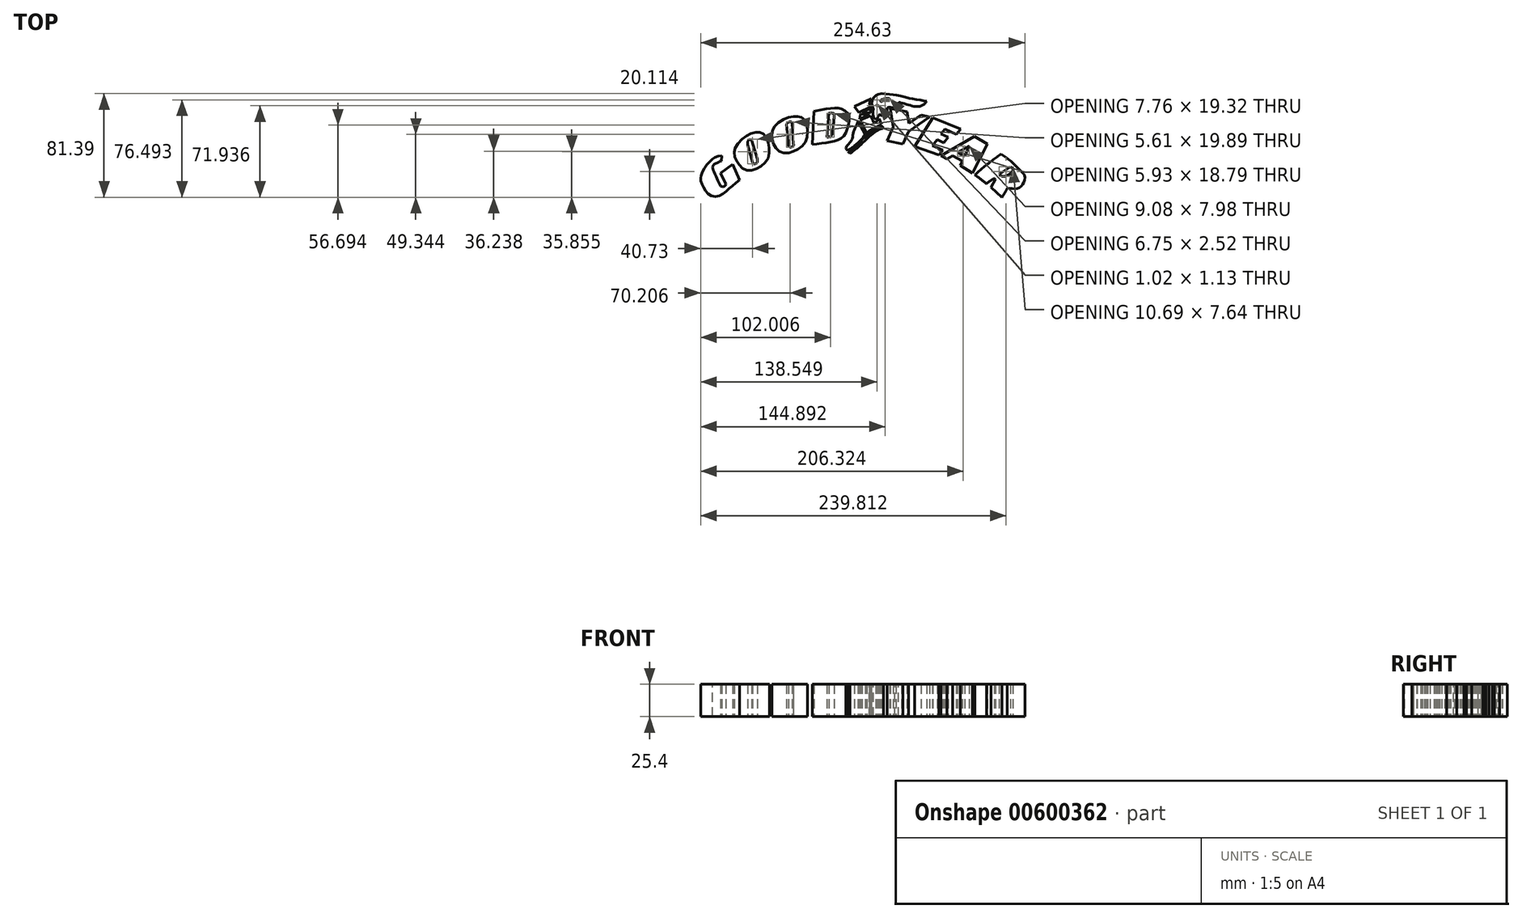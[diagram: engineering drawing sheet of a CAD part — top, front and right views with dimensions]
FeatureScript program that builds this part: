
annotation { "Feature Type Name" : "Feature", "Feature Type Description" : "" }
export const myFeature = defineFeature(function(context is Context, id is Id, definition is map)
    precondition{}
    {
        {
            var Q0;
            Q0=qCreatedBy(makeId("Top.planeOp"),FACE);
            var sketch = newSketch(context, id + "F0", { "sketchPlane" : qUnion([Q0])});
            skFitSpline(sketch, "E0", {"points": [v(-59.77, 19.65) * mm, v(-63.83, 18.9) * mm, v(-66.56, 17.29) * mm, v(-70.08, 14) * mm, v(-73.2, 9.83) * mm, v(-75.73, 4.75) * mm, v(-76.25, 2.47) * mm, v(-76.18, 0) * mm, v(-74.98, -3.55) * mm, v(-72.37, -7.96) * mm, v(-69.17, -11.16) * mm, v(-64.56, -12.56) * mm, v(-59.15, -10.76) * mm, v(-55.35, -7.59) * mm, v(-51.14, -3.95) * mm, v(-45.8, 0.36) * mm], "startDerivative": vector(-48.72, 2.07) * mm, "endDerivative": vector(63.75, 50.3) * mm});
            skLineSegment(sketch, "E1", {"start": v(-59.77, 19.65) * mm, "end": v(-59.86, 15.48) * mm});
            skLineSegment(sketch, "E2", {"start": v(-45.8, 0.36) * mm, "end": v(-51.25, 12.96) * mm});
            skLineSegment(sketch, "E3", {"start": v(-51.25, 12.96) * mm, "end": v(-60.63, 5.88) * mm});
            skLineSegment(sketch, "E4", {"start": v(-60.63, 5.88) * mm, "end": v(-56.41, -2.7) * mm});
            skFitSpline(sketch, "E5", {"points": [v(-59.86, 15.48) * mm, v(-62.4, 14.45) * mm, v(-64.42, 13.43) * mm, v(-66.28, 12.15) * mm, v(-66.87, 9.93) * mm, v(-66.03, 7.47) * mm, v(-64, 2.8) * mm, v(-62.32, -0.84) * mm, v(-61.06, -3.39) * mm, v(-60.55, -4.32) * mm, v(-58.95, -4.91) * mm, v(-57.09, -4.06) * mm, v(-56.41, -2.7) * mm], "startDerivative": vector(-29.78, -11.35) * mm, "endDerivative": vector(6.97, 21.82) * mm});
            skFitSpline(sketch, "E6", {"points": [v(-49.9, 22.3) * mm, v(-48.7, 26.42) * mm, v(-44.08, 32.4) * mm, v(-38.41, 36.27) * mm, v(-33.27, 38.01) * mm, v(-29.32, 37.9) * mm, v(-25.5, 35.12) * mm, v(-23.13, 29.56) * mm, v(-22.34, 23.86) * mm, v(-23.27, 17.75) * mm, v(-27.62, 12.43) * mm, v(-32.9, 9.1) * mm, v(-38.3, 7.89) * mm, v(-43.44, 9.73) * mm, v(-46.87, 13.56) * mm, v(-48.97, 17.14) * mm, v(-49.9, 22.3) * mm]});
            skLineSegment(sketch, "E7", {"start": v(-36.05, 31.72) * mm, "end": v(-31.85, 16.84) * mm});
            skLineSegment(sketch, "E8", {"start": v(-39.36, 28.04) * mm, "end": v(-35.4, 14.58) * mm});
            skFitSpline(sketch, "E9", {"points": [v(-39.36, 28.04) * mm, v(-39.36, 30.3) * mm, v(-38.28, 31.96) * mm, v(-36.88, 32.38) * mm, v(-36.05, 31.72) * mm], "startDerivative": vector(-0.89, 7.93) * mm, "endDerivative": vector(3.61, -4.33) * mm});
            skFitSpline(sketch, "E10", {"points": [v(-31.85, 16.84) * mm, v(-31.85, 14.17) * mm, v(-33.09, 13.34) * mm, v(-34.41, 13.08) * mm, v(-35.4, 14.58) * mm], "startDerivative": vector(1.44, -10.29) * mm, "endDerivative": vector(-1.3, 7.85) * mm});
            skLineSegment(sketch, "E11", {"start": v(-8.9, 44.2) * mm, "end": v(-7.35, 27.45) * mm});
            skLineSegment(sketch, "E12", {"start": v(-4.4, 45.2) * mm, "end": v(-3.4, 28.77) * mm});
            skFitSpline(sketch, "E13", {"points": [v(-8.9, 44.2) * mm, v(-8.13, 45.2) * mm, v(-6.65, 46.05) * mm, v(-5.18, 46.05) * mm, v(-4.4, 45.2) * mm], "startDerivative": vector(2.8, 4.36) * mm, "endDerivative": vector(2.83, -4.51) * mm});
            skFitSpline(sketch, "E14", {"points": [v(-7.35, 27.45) * mm, v(-6.5, 26.52) * mm, v(-5.65, 26.29) * mm, v(-4.64, 26.44) * mm, v(-3.4, 27.3) * mm, v(-3.4, 28.77) * mm], "startDerivative": vector(3.78, -5) * mm, "endDerivative": vector(-0.95, 4.32) * mm});
            skFitSpline(sketch, "E15", {"points": [v(-18.2, 42.64) * mm, v(-12.62, 47.37) * mm, v(-6.27, 49.93) * mm, v(-1.3, 50.4) * mm, v(2.34, 49.85) * mm, v(5.9, 47.3) * mm, v(7.53, 39.7) * mm, v(6.83, 32.33) * mm, v(4.12, 27.53) * mm, v(-1.46, 23.89) * mm, v(-6.11, 21.87) * mm, v(-12.23, 22.1) * mm, v(-16.34, 24.5) * mm, v(-18.82, 28.46) * mm, v(-20.22, 33.88) * mm, v(-19.9, 39.39) * mm, v(-18.2, 42.64) * mm]});
            skLineSegment(sketch, "E16", {"start": v(11.4, 28.26) * mm, "end": v(12.75, 54.33) * mm});
            skFitSpline(sketch, "E17", {"points": [v(12.75, 54.33) * mm, v(20.03, 55.86) * mm, v(28.5, 57.04) * mm, v(34.08, 56.36) * mm, v(39.5, 52.64) * mm, v(40.17, 45.53) * mm, v(38.14, 38.42) * mm, v(34.59, 33.68) * mm, v(28.83, 31.14) * mm, v(21.05, 29.62) * mm, v(11.4, 28.26) * mm], "startDerivative": vector(68.9, 15.11) * mm, "endDerivative": vector(-84.89, -11.4) * mm});
            skLineSegment(sketch, "E18", {"start": v(24.6, 52.98) * mm, "end": v(22.74, 34.19) * mm});
            skFitSpline(sketch, "E19", {"points": [v(24.6, 52.98) * mm, v(27.14, 52.98) * mm, v(28.44, 52.5) * mm, v(28.64, 50.15) * mm, v(27.66, 41.03) * mm, v(26.74, 36.1) * mm, v(26.16, 35.14) * mm, v(25.17, 34.46) * mm, v(22.74, 34.19) * mm], "startDerivative": vector(22.33, 0.87) * mm, "endDerivative": vector(-23, -0.54) * mm});
            skFitSpline(sketch, "E20", {"points": [v(39.1, 23.6) * mm, v(44.18, 27) * mm, v(48.7, 31.12) * mm, v(50.89, 33.22) * mm, v(51.7, 34.88) * mm, v(52.92, 36) * mm], "startDerivative": vector(19.7, 11.7) * mm, "endDerivative": vector(13.38, 3.84) * mm});
            skLineSegment(sketch, "E21", {"start": v(47.46, 46.57) * mm, "end": v(52.92, 36) * mm});
            skFitSpline(sketch, "E22", {"points": [v(47.46, 46.57) * mm, v(46.54, 44.19) * mm, v(45.11, 41.5) * mm, v(43.53, 37) * mm, v(42.43, 32.07) * mm, v(39.8, 28.44) * mm, v(38.07, 26.31) * mm, v(37.96, 24.84) * mm, v(39.1, 23.6) * mm], "startDerivative": vector(-7.2, -21.21) * mm, "endDerivative": vector(15.31, -12.42) * mm});
            skLineSegment(sketch, "E23", {"start": v(40.96, 21.31) * mm, "end": v(39.53, 22.69) * mm});
            skLineSegment(sketch, "E24", {"start": v(65.88, 43.08) * mm, "end": v(67.2, 41.3) * mm});
            skFitSpline(sketch, "E25", {"points": [v(65.88, 43.08) * mm, v(64.37, 42.22) * mm, v(62.42, 41.22) * mm, v(59.63, 39.5) * mm, v(56.94, 37.62) * mm, v(53.71, 35.18) * mm, v(48.96, 30.47) * mm, v(47.97, 29.32) * mm, v(46.11, 27.54) * mm, v(43.82, 25.45) * mm, v(41.44, 24.06) * mm, v(39.53, 22.69) * mm], "startDerivative": vector(-17.38, -20) * mm, "endDerivative": vector(-22.35, -17.46) * mm});
            skFitSpline(sketch, "E26", {"points": [v(67.2, 41.3) * mm, v(66, 40.84) * mm, v(64.5, 40.51) * mm, v(62.4, 39.36) * mm, v(58.05, 36.12) * mm, v(53.94, 32.64) * mm, v(49.63, 28.21) * mm, v(46.94, 25.96) * mm, v(44.17, 23.59) * mm, v(40.96, 21.31) * mm], "startDerivative": vector(-16.72, -16.2) * mm, "endDerivative": vector(-28.08, -18.76) * mm});
            skLineSegment(sketch, "E27", {"start": v(47.81, 53.38) * mm, "end": v(44.5, 58.28) * mm});
            skLineSegment(sketch, "E28", {"start": v(44.5, 58.28) * mm, "end": v(57.43, 64.4) * mm});
            skLineSegment(sketch, "E29", {"start": v(47.81, 53.38) * mm, "end": v(57.06, 57.79) * mm});
            skFitSpline(sketch, "E30", {"points": [v(57.43, 64.4) * mm, v(56.51, 62.01) * mm, v(56.51, 59.2) * mm, v(57.06, 57.79) * mm], "startDerivative": vector(-3.12, -6.33) * mm, "endDerivative": vector(2.33, -4.57) * mm});
            skLineSegment(sketch, "E31", {"start": v(50.63, 53.74) * mm, "end": v(57.69, 57.09) * mm});
            skLineSegment(sketch, "E32", {"start": v(50.63, 53.74) * mm, "end": v(57.3, 53.2) * mm});
            skFitSpline(sketch, "E33", {"points": [v(57.69, 57.09) * mm, v(57.17, 55.72) * mm, v(57.3, 53.2) * mm], "startDerivative": vector(-2.15, -4.28) * mm, "endDerivative": vector(1.5, -3.48) * mm});
            skLineSegment(sketch, "E34", {"start": v(48.55, 48.32) * mm, "end": v(49.17, 52.19) * mm});
            skLineSegment(sketch, "E35", {"start": v(49.17, 52.19) * mm, "end": v(56.3, 51.91) * mm});
            skLineSegment(sketch, "E36", {"start": v(48.55, 48.32) * mm, "end": v(56.3, 51.91) * mm});
            skLineSegment(sketch, "E37", {"start": v(48.94, 47.29) * mm, "end": v(54.3, 36.9) * mm});
            skLineSegment(sketch, "E38", {"start": v(48.94, 47.29) * mm, "end": v(57.19, 51.08) * mm});
            skLineSegment(sketch, "E39", {"start": v(57.19, 51.08) * mm, "end": v(58.36, 48.52) * mm});
            skFitSpline(sketch, "E40", {"points": [v(58.36, 48.52) * mm, v(59.08, 46.84) * mm, v(59.66, 45.79) * mm, v(61.14, 45.98) * mm, v(63.83, 48.86) * mm], "startDerivative": vector(3.27, -7.15) * mm, "endDerivative": vector(7.57, 10.06) * mm});
            skLineSegment(sketch, "E41", {"start": v(63.83, 48.86) * mm, "end": v(65.82, 44.11) * mm});
            skFitSpline(sketch, "E42", {"points": [v(54.3, 36.9) * mm, v(55.69, 38.57) * mm, v(60.65, 41.48) * mm, v(65.82, 44.11) * mm], "startDerivative": vector(4.45, 7) * mm, "endDerivative": vector(13.02, 6.62) * mm});
            skFitSpline(sketch, "E43", {"points": [v(61.18, 48.14) * mm, v(59.75, 49.36) * mm, v(58.81, 53.55) * mm, v(59.36, 56.2) * mm, v(58.43, 58.46) * mm, v(58.43, 62.76) * mm, v(60.3, 66.01) * mm, v(63.28, 67.89) * mm, v(68.08, 68.22) * mm, v(73.92, 67.61) * mm, v(78.94, 66.95) * mm, v(86.83, 64.74) * mm, v(91.57, 63.97) * mm, v(97.08, 63.03) * mm, v(101.33, 62.43) * mm], "startDerivative": vector(-31.99, 17.8) * mm, "endDerivative": vector(56.5, -7.36) * mm});
            skFitSpline(sketch, "E44", {"points": [v(101.33, 62.43) * mm, v(98.46, 59.34) * mm, v(94.1, 58.18) * mm, v(88.87, 58.9) * mm, v(84.12, 60.28) * mm, v(81.15, 61.1) * mm, v(79.88, 61.54) * mm, v(79.16, 60.94) * mm, v(79.71, 60.39) * mm, v(80.65, 59.9) * mm, v(81.75, 59.72) * mm], "startDerivative": vector(-19.3, -26.52) * mm, "endDerivative": vector(16.87, -1.16) * mm});
            skFitSpline(sketch, "E45", {"points": [v(81.75, 59.72) * mm, v(79.88, 58.68) * mm, v(78, 58.73) * mm, v(76.46, 58.95) * mm, v(76.4, 58.24) * mm, v(77.18, 57.85) * mm], "startDerivative": vector(-7.43, -5.2) * mm, "endDerivative": vector(5.92, -1.38) * mm});
            skFitSpline(sketch, "E46", {"points": [v(77.18, 57.85) * mm, v(76.35, 57.32) * mm, v(74.43, 57.29) * mm, v(72.68, 57.62) * mm, v(70.63, 57.45) * mm, v(70.2, 54.94) * mm, v(69.4, 53.45) * mm, v(67.58, 53.5) * mm, v(66.48, 51.67) * mm, v(65.59, 51) * mm, v(64.36, 51.84) * mm, v(63.05, 50.4) * mm, v(62.37, 48.62) * mm, v(61.18, 48.14) * mm], "startDerivative": vector(-11.9, -10.87) * mm, "endDerivative": vector(-16.98, 9.93) * mm});
            skFitSpline(sketch, "E47", {"points": [v(61.74, 59.24) * mm, v(62.63, 59.24) * mm, v(62.65, 58.37) * mm, v(62.19, 58.35) * mm, v(62.32, 58.84) * mm, v(61.9, 58.82) * mm, v(61.74, 59.24) * mm]});
            skFitSpline(sketch, "E48", {"points": [v(65.21, 62.9) * mm, v(66.4, 63.76) * mm, v(68.44, 64.34) * mm, v(70.3, 64.56) * mm, v(71.94, 64.47) * mm, v(71.87, 63.65) * mm, v(69.29, 63.25) * mm, v(66.9, 62.78) * mm, v(66.02, 62.18) * mm, v(65.15, 62.25) * mm, v(65.21, 62.9) * mm]});
            skLineSegment(sketch, "E49", {"start": v(72.66, 56.7) * mm, "end": v(75.06, 41.97) * mm});
            skLineSegment(sketch, "E50", {"start": v(75.06, 41.97) * mm, "end": v(70.23, 31.2) * mm});
            skLineSegment(sketch, "E51", {"start": v(70.23, 31.2) * mm, "end": v(82.54, 28.69) * mm});
            skLineSegment(sketch, "E52", {"start": v(82.54, 28.69) * mm, "end": v(87, 38.62) * mm});
            skLineSegment(sketch, "E53", {"start": v(87, 38.62) * mm, "end": v(103.68, 50.06) * mm});
            skLineSegment(sketch, "E54", {"start": v(103.68, 50.06) * mm, "end": v(96.8, 51.47) * mm});
            skLineSegment(sketch, "E55", {"start": v(96.8, 51.47) * mm, "end": v(87.33, 44.97) * mm});
            skLineSegment(sketch, "E56", {"start": v(87.33, 44.97) * mm, "end": v(85.86, 54) * mm});
            skLineSegment(sketch, "E57", {"start": v(85.86, 54) * mm, "end": v(72.66, 56.7) * mm});
            skLineSegment(sketch, "E58", {"start": v(91.9, 26.82) * mm, "end": v(106.1, 49.42) * mm});
            skLineSegment(sketch, "E59", {"start": v(106.1, 49.42) * mm, "end": v(128.08, 40.3) * mm});
            skLineSegment(sketch, "E60", {"start": v(128.08, 40.3) * mm, "end": v(124.49, 36.46) * mm});
            skLineSegment(sketch, "E61", {"start": v(124.49, 36.46) * mm, "end": v(115.55, 40.57) * mm});
            skLineSegment(sketch, "E62", {"start": v(115.55, 40.57) * mm, "end": v(112.49, 36.8) * mm});
            skLineSegment(sketch, "E63", {"start": v(112.49, 36.8) * mm, "end": v(118.1, 34.18) * mm});
            skLineSegment(sketch, "E64", {"start": v(118.1, 34.18) * mm, "end": v(114.68, 29.54) * mm});
            skLineSegment(sketch, "E65", {"start": v(114.68, 29.54) * mm, "end": v(109.42, 32.16) * mm});
            skLineSegment(sketch, "E66", {"start": v(109.42, 32.16) * mm, "end": v(105.74, 27.43) * mm});
            skLineSegment(sketch, "E67", {"start": v(105.74, 27.43) * mm, "end": v(114.15, 24.02) * mm});
            skLineSegment(sketch, "E68", {"start": v(114.15, 24.02) * mm, "end": v(110.82, 20) * mm});
            skLineSegment(sketch, "E69", {"start": v(110.82, 20) * mm, "end": v(91.9, 26.82) * mm});
            skLineSegment(sketch, "E70", {"start": v(112.29, 19.53) * mm, "end": v(138.65, 34.6) * mm});
            skLineSegment(sketch, "E71", {"start": v(138.65, 34.6) * mm, "end": v(149.02, 28.7) * mm});
            skLineSegment(sketch, "E72", {"start": v(149.02, 28.7) * mm, "end": v(137.16, 5.95) * mm});
            skLineSegment(sketch, "E73", {"start": v(137.16, 5.95) * mm, "end": v(127.55, 11.85) * mm});
            skLineSegment(sketch, "E74", {"start": v(127.55, 11.85) * mm, "end": v(129.33, 15.35) * mm});
            skLineSegment(sketch, "E75", {"start": v(129.33, 15.35) * mm, "end": v(121.52, 19.59) * mm});
            skLineSegment(sketch, "E76", {"start": v(121.52, 19.59) * mm, "end": v(117.2, 16.87) * mm});
            skLineSegment(sketch, "E77", {"start": v(117.2, 16.87) * mm, "end": v(112.29, 19.53) * mm});
            skLineSegment(sketch, "E78", {"start": v(125.49, 22.15) * mm, "end": v(134.56, 27.12) * mm});
            skLineSegment(sketch, "E79", {"start": v(134.56, 27.12) * mm, "end": v(131.04, 19.14) * mm});
            skLineSegment(sketch, "E80", {"start": v(131.04, 19.14) * mm, "end": v(125.49, 22.15) * mm});
            skFitSpline(sketch, "E81", {"points": [v(139.14, 4.57) * mm, v(145.18, 9.89) * mm, v(153.62, 16.45) * mm, v(159.77, 20.93) * mm], "startDerivative": vector(17.67, 16.08) * mm, "endDerivative": vector(18.73, 13.48) * mm});
            skFitSpline(sketch, "E82", {"points": [v(159.77, 20.93) * mm, v(168.42, 14.37) * mm, v(174.98, 7.8) * mm, v(178.1, 3.84) * mm, v(177.07, -2.4) * mm, v(172.06, -6.16) * mm, v(164.56, -5.74) * mm], "startDerivative": vector(44.5, -30.97) * mm, "endDerivative": vector(-46.73, 8.55) * mm});
            skFitSpline(sketch, "E83", {"points": [v(164.56, -5.74) * mm, v(162.69, -9.4) * mm, v(160.38, -13.1) * mm], "startDerivative": vector(-3.62, -7.3) * mm, "endDerivative": vector(-4.1, -6.66) * mm});
            skFitSpline(sketch, "E84", {"points": [v(139.14, 4.57) * mm, v(143.4, 1.34) * mm, v(148.2, -2.4) * mm], "startDerivative": vector(8.71, -6.53) * mm, "endDerivative": vector(9.4, -7.42) * mm});
            skFitSpline(sketch, "E85", {"points": [v(148.2, -2.4) * mm, v(150.73, -0.48) * mm, v(154.35, 1.86) * mm], "startDerivative": vector(4.88, 2.85) * mm, "endDerivative": vector(7.3, 5.55) * mm});
            skLineSegment(sketch, "E86", {"start": v(154.35, 1.86) * mm, "end": v(155.3, 1.04) * mm});
            skLineSegment(sketch, "E87", {"start": v(155.3, 1.04) * mm, "end": v(151.65, -5.27) * mm});
            skLineSegment(sketch, "E88", {"start": v(151.65, -5.27) * mm, "end": v(160.38, -13.1) * mm});
            skLineSegment(sketch, "E89", {"start": v(158.17, 4.93) * mm, "end": v(167, 10.82) * mm});
            skFitSpline(sketch, "E90", {"points": [v(167, 10.82) * mm, v(168.9, 9.08) * mm, v(167.83, 6.42) * mm, v(164.02, 3.8) * mm, v(161.31, 3.23) * mm, v(158.17, 4.93) * mm], "startDerivative": vector(14.19, -8.55) * mm, "endDerivative": vector(-15.28, 10.77) * mm});
            skSolve(sketch);
        }
        {
            var Q0;
            Q0=qSketchRegion(id+"F0",true);
            extrude(context, id + "F1", {"entities" : qUnion([Q0]), "depth" : 25.4 * mm, "offsetDistance" : 25.4 * mm});
        }
    });
